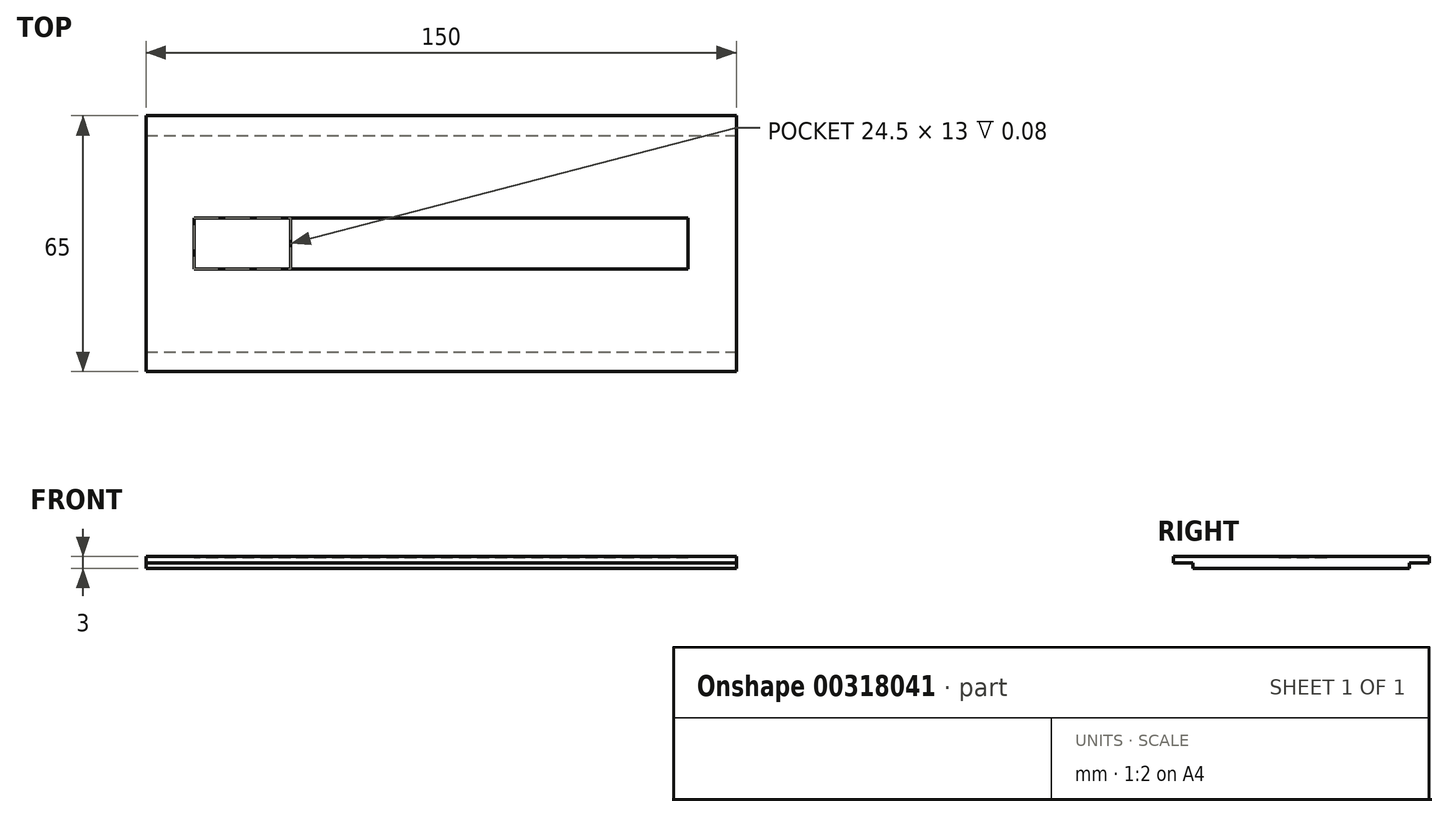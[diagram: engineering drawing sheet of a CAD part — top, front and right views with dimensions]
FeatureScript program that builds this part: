
annotation { "Feature Type Name" : "Feature", "Feature Type Description" : "" }
export const myFeature = defineFeature(function(context is Context, id is Id, definition is map)
    precondition{}
    {
        {
            var Q0;
            Q0=qCreatedBy(makeId("Top.planeOp"),FACE);
            var sketch = newSketch(context, id + "F0", { "sketchPlane" : qUnion([Q0])});
            skLineSegment(sketch, "E0.bottom", {"start": v(75, 32.5) * mm, "end": v(-75, 32.5) * mm});
            skLineSegment(sketch, "E0.top", {"start": v(75, -32.5) * mm, "end": v(-75, -32.5) * mm});
            skLineSegment(sketch, "E0.left", {"start": v(75, 32.5) * mm, "end": v(75, -32.5) * mm});
            skLineSegment(sketch, "E0.right", {"start": v(-75, 32.5) * mm, "end": v(-75, -32.5) * mm});
            skPoint(sketch, "E0.middle", {"position": v(0, 0) * mm});
            skSolve(sketch);
        }
        {
            var Q0;
            Q0=makeQuery(id+"F0.imprint","IMPRINT",FACE,{"disambiguationData":[TD([[makeQuery(id+"F0.imprint","IMPRINT",EDGE,{"derivedFrom":sQuery(id+"F0.wireOp",EDGE,"E0.bottom")}),1.0]])]});
            extrude(context, id + "F1", {"entities" : qUnion([Q0]), "depth" : 3 * mm});
        }
        {
            var Q0;
            Q0=makeQuery(id+"F1.opExtrude","CAP_FACE",FACE,{"disambiguationData":[OSD([sQuery(id+"F0.wireOp",EDGE,"E0.bottom"),sQuery(id+"F0.wireOp",EDGE,"E0.top"),sQuery(id+"F0.wireOp",EDGE,"E0.left"),sQuery(id+"F0.wireOp",EDGE,"E0.right")])],"isStart":false});
            var sketch = newSketch(context, id + "F2", { "sketchPlane" : qUnion([Q0])});
            skLineSegment(sketch, "E1.bottom", {"start": v(62.75, 6.5) * mm, "end": v(-62.75, 6.5) * mm});
            skLineSegment(sketch, "E1.top", {"start": v(62.75, -6.5) * mm, "end": v(-62.75, -6.5) * mm});
            skLineSegment(sketch, "E1.left", {"start": v(62.75, 6.5) * mm, "end": v(62.75, -6.5) * mm});
            skLineSegment(sketch, "E1.right", {"start": v(-62.75, 6.5) * mm, "end": v(-62.75, -6.5) * mm});
            skPoint(sketch, "E1.middle", {"position": v(0, 0) * mm});
            skLineSegment(sketch, "E2", {"start": v(-38.25, 6.5) * mm, "end": v(-38.25, -6.5) * mm});
            skLineSegment(sketch, "E3.bottom", {"start": v(-38.25, 6.5) * mm, "end": v(62.75, 6.5) * mm});
            skLineSegment(sketch, "E3.top", {"start": v(-38.25, 8.2) * mm, "end": v(62.75, 8.2) * mm});
            skLineSegment(sketch, "E3.left", {"start": v(-38.25, 6.5) * mm, "end": v(-38.25, 8.2) * mm});
            skLineSegment(sketch, "E3.right", {"start": v(62.75, 6.5) * mm, "end": v(62.75, 8.2) * mm});
            skSolve(sketch);
        }
        {
            var Q0;
            Q0=makeQuery(id+"F1.opExtrude","SWEPT_FACE",FACE,{"disambiguationData":[OSD([sQuery(id+"F0.wireOp",EDGE,"E0.left")])]});
            var sketch = newSketch(context, id + "F3", { "sketchPlane" : qUnion([Q0])});
            skLineSegment(sketch, "E4.bottom", {"start": v(-32.5, 0) * mm, "end": v(-27.5, 0) * mm});
            skLineSegment(sketch, "E4.top", {"start": v(-32.5, 1.4) * mm, "end": v(-27.5, 1.4) * mm});
            skLineSegment(sketch, "E4.left", {"start": v(-32.5, 0) * mm, "end": v(-32.5, 1.4) * mm});
            skLineSegment(sketch, "E4.right", {"start": v(-27.5, 0) * mm, "end": v(-27.5, 1.4) * mm});
            skLineSegment(sketch, "E5.MirrorCS", {"start": v(32.5, 0) * mm, "end": v(32.5, 1.4) * mm});
            skLineSegment(sketch, "E6.MirrorCS", {"start": v(27.5, 0) * mm, "end": v(27.5, 1.4) * mm});
            skLineSegment(sketch, "E7.MirrorCS", {"start": v(32.5, 0) * mm, "end": v(27.5, 0) * mm});
            skLineSegment(sketch, "E8.MirrorCS", {"start": v(32.5, 1.4) * mm, "end": v(27.5, 1.4) * mm});
            skSolve(sketch);
        }
        {
            var Q0;
            Q0 = qSketchRegion(id + "F3", true);
            extrude(context, id + "F4", {"entities" : qUnion([Q0]), "operationType" : NewBodyOperationType.REMOVE, "endBound" : BoundingType.THROUGH_ALL, "oppositeDirection" : true, "depth" : 25 * mm});
        }
        {
            var Q0;
            {var subQ0=sQuery(id+"F2.wireOp",EDGE,"E1.left");Q0=makeQuery(id+"F2.imprint","IMPRINT",FACE,{"disambiguationData":[TD([[makeQuery(id+"F2.imprint","IMPRINT",EDGE,{"derivedFrom":subQ0}),-1.0]])]});}
            var Q1;
            Q1=makeQuery(id+"F2.imprint","IMPRINT",FACE,{"disambiguationData":[TD([[makeQuery(id+"F2.imprint","IMPRINT",EDGE,{"derivedFrom":sQuery(id+"F2.wireOp",EDGE,"E3.bottom")}),1.0]])]});
            extrude(context, id + "F5", {"entities" : qUnion([Q0, Q1]), "operationType" : NewBodyOperationType.REMOVE, "oppositeDirection" : true, "depth" : .35 * mm});
        }
        {
            var Q0;
            {var subQ0=sQuery(id+"F2.wireOp",EDGE,"E1.right");Q0=makeQuery(id+"F2.imprint","IMPRINT",FACE,{"disambiguationData":[TD([[makeQuery(id+"F2.imprint","IMPRINT",EDGE,{"derivedFrom":subQ0}),1.0]])]});}
            extrude(context, id + "F6", {"entities" : qUnion([Q0]), "operationType" : NewBodyOperationType.REMOVE, "oppositeDirection" : true, "depth" : .43 * mm});
        }
    });
